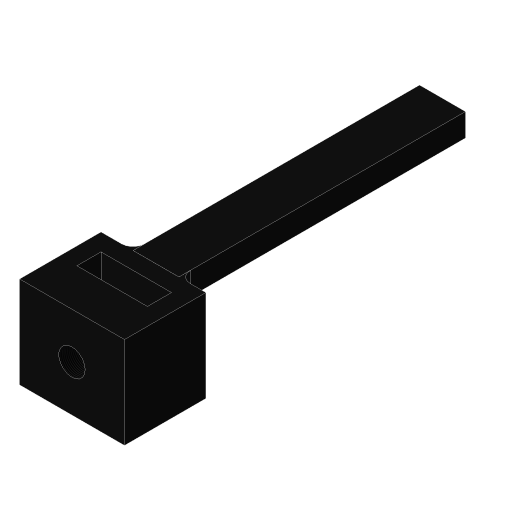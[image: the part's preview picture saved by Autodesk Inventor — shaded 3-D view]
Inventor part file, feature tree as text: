
AUTODESK INVENTOR PART (.ipt)
format: ipt  version: 2023 (Build 270158000, 158)  size: 122,368 bytes
history: native  units: mm
features: sketch x4, extrude x3, fillet x1, thread x1
ambient origin geometry x8: Origin, YZ Plane, XZ Plane, XY Plane, X Axis, Y Axis, Z Axis, Center Point
bodies: Solid1 (feature_tree)
feature tree (9):
  extrude  "Extrusion1"  Depth=2.1mm
  extrude  "Extrusion4"  Depth=8.0mm TaperAngle=0.0deg
  sketch  "3D Sketch1"
  extrude  "Extrusion5"  Depth=3.5mm
  fillet  "Fillet1"  Radius=4.0mm
  thread  "Thread1"  [1 undecoded]
  sketch  "Sketch1"  dims[d0=6.15mm d1=2.1mm]
  sketch  "Sketch4"  dims[d2=1.5mm d3=8.0mm d4=0.0mm]
  sketch  "Sketch5"  dims[d12=2.0mm d13=2.3mm d14=4.0mm d15=0.0mm d16=4.0mm d17=2.0mm d18=25.0mm d19=0.0mm d20=1.0mm d21=3.5mm d22=0.0mm]
note: 1 required parameter value undecoded (feature->parameter linkage not recoverable at this tier; creation-order binding heuristic only, values carry confidence <= 0.55)
